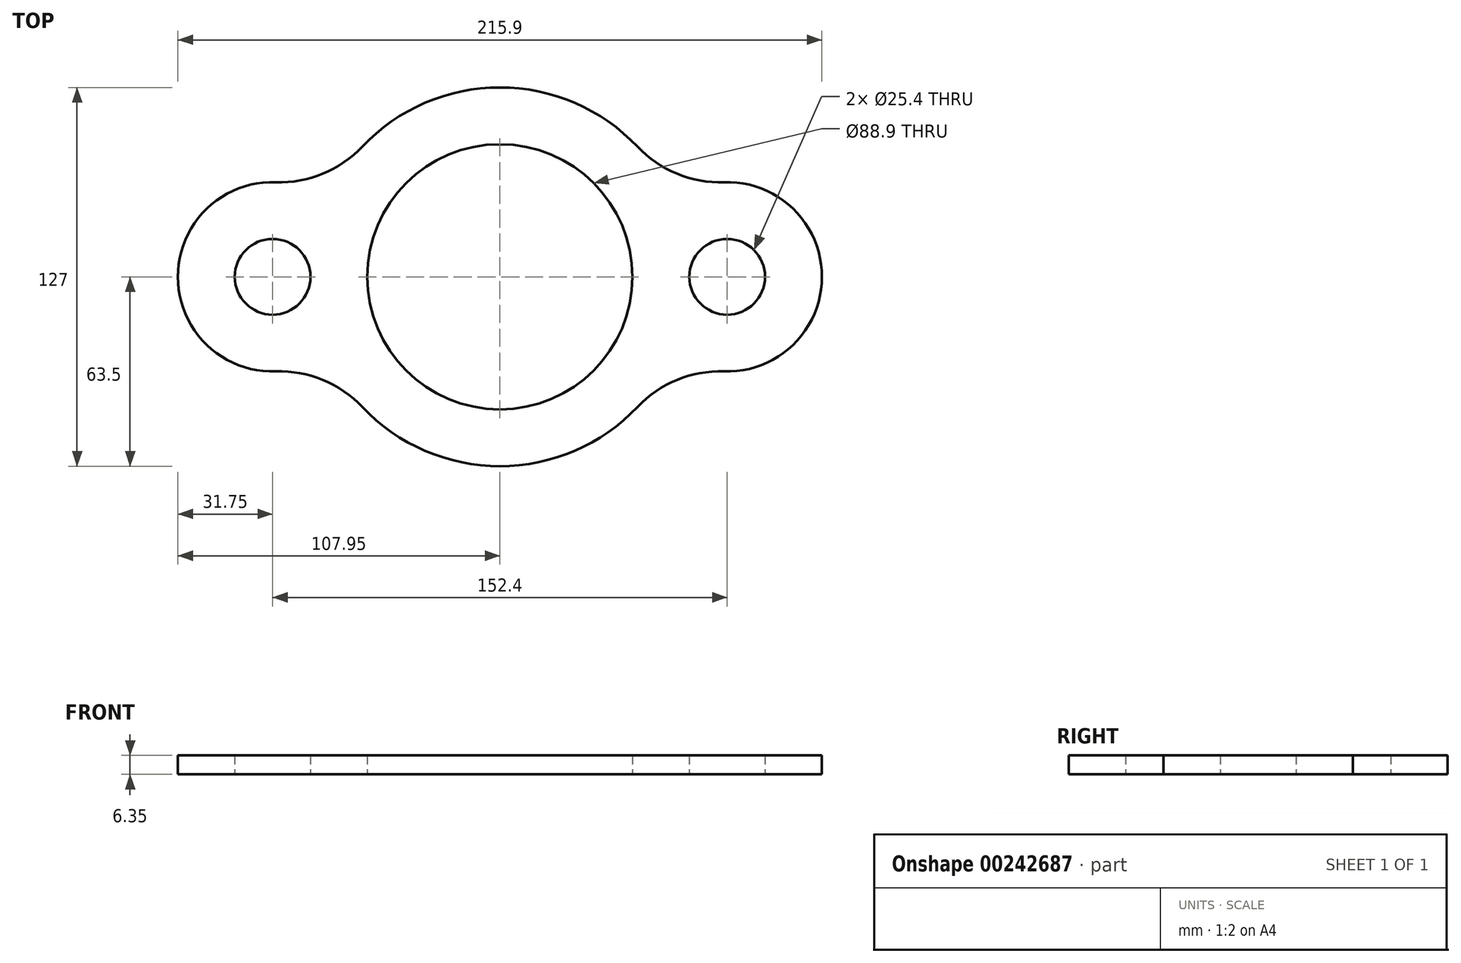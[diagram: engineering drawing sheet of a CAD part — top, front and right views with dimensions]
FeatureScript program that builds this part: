
annotation { "Feature Type Name" : "Feature", "Feature Type Description" : "" }
export const myFeature = defineFeature(function(context is Context, id is Id, definition is map)
    precondition{}
    {
        {
            var Q0;
            Q0=qCreatedBy(makeId("Top.planeOp"),FACE);
            var sketch = newSketch(context, id + "F0", { "sketchPlane" : qUnion([Q0])});
            skCircle(sketch, "E0", {"center": v(0, 0) * mm, "radius": 44.45 * mm});
            skArc(sketch, "E1", {"start": v(-46.14, -43.63) * mm, "mid": v(0, -63.5) * mm, "end": v(46.14, -43.63) * mm});
            skCircle(sketch, "E2", {"center": v(-76.2, 0) * mm, "radius": 12.7 * mm});
            skArc(sketch, "E3", {"start": v(-75.12, 31.73) * mm, "mid": v(-107.95, 0) * mm, "end": v(-75.12, -31.73) * mm});
            skArc(sketch, "E4.MirrorC", {"start": v(75.12, 31.73) * mm, "mid": v(107.95, 0) * mm, "end": v(75.12, -31.73) * mm});
            skCircle(sketch, "E5.MirrorC", {"center": v(76.2, 0) * mm, "radius": 12.7 * mm});
            skArc(sketch, "E6.trimOffspring", {"start": v(46.14, 43.63) * mm, "mid": v(0, 63.5) * mm, "end": v(-46.14, 43.63) * mm});
            skPoint(sketch, "E7.visualSharp", {"position": v(-57.94, 25.98) * mm});
            skArc(sketch, "E7.filletArc", {"start": v(-75.12, 31.73) * mm, "mid": v(-59.35, 34.56) * mm, "end": v(-46.14, 43.63) * mm});
            skPoint(sketch, "E8.visualSharp", {"position": v(57.94, 25.98) * mm});
            skArc(sketch, "E8.filletArc", {"start": v(46.14, 43.63) * mm, "mid": v(59.35, 34.56) * mm, "end": v(75.12, 31.73) * mm});
            skPoint(sketch, "E9.visualSharp", {"position": v(57.94, -25.98) * mm});
            skArc(sketch, "E9.filletArc", {"start": v(75.12, -31.73) * mm, "mid": v(59.35, -34.56) * mm, "end": v(46.14, -43.63) * mm});
            skPoint(sketch, "E10.visualSharp", {"position": v(-57.94, -25.98) * mm});
            skArc(sketch, "E10.filletArc", {"start": v(-46.14, -43.63) * mm, "mid": v(-59.35, -34.56) * mm, "end": v(-75.12, -31.73) * mm});
            skSolve(sketch);
        }
        {
            var Q0;
            Q0=makeQuery(id+"F0.imprint","IMPRINT",FACE,{"disambiguationData":[TD([[makeQuery(id+"F0.imprint","IMPRINT",EDGE,{"derivedFrom":sQuery(id+"F0.wireOp",EDGE,"E0")}),-1.0]])]});
            extrude(context, id + "F1", {"entities" : qUnion([Q0]), "depth" : 6.35 * mm});
        }
    });
